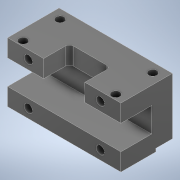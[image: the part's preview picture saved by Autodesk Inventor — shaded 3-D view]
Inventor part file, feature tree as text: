
AUTODESK INVENTOR PART (.ipt)
format: ipt  version: 2021 (Build 250183000, 183)  size: 206,336 bytes
history: native  units: mm
features: sketch x8, other x6, extrude x5, hole x3, fillet x1
ambient origin geometry x8: Origin, YZ Plane, XZ Plane, XY Plane, X Axis, Y Axis, Z Axis, Center Point
bodies: Body1 (feature_tree)
feature tree (23):
  other  "Sólido1"
  extrude  "Extrusão1"  Depth=25.0mm
  extrude  "Extrusão2"  Depth=8.0mm
  extrude  "Extrusão3"  Depth=15.0mm
  extrude  "Extrusão4"  Depth=8.5mm
  hole  "Furo1"  [1 undecoded]
  extrude  "Extrusão5"  Depth=5.0mm
  fillet  "Arredondamento1"  Radius=27.5mm
  hole  "Furo3"  [1 undecoded]
  other  "Plano de trabalho2"
  hole  "Furo4"  [1 undecoded]
  sketch  "Esboço1"  dims[d0=35.0mm d1=25.0mm]
  sketch  "Esboço2"  dims[d2=55.0mm d3=0.0mm d4=8.0mm]
  sketch  "Esboço3"  dims[d5=1.5mm d6=0.0mm d7=15.0mm]
  sketch  "Esboço4"  dims[d8=12.0mm d9=8.5mm]
  sketch  "Esboço5"  dims[d10=0.0mm d11=0.0mm d12=8.5mm]
  other  "Contorno projetado1"
  sketch  "Esboço6"  dims[d13=0.0mm d14=0.0mm d15=5.0mm d16=27.5mm]
  sketch  "Esboço8"  dims[d17=10.0mm d18=10.0mm]
  other  "Contorno projetado4"
  sketch  "Esboço9"  dims[d19=4.0mm d20=6.0mm d21=4.0mm d22=2.0mm d23=90.0deg d24=5.0mm d25=0.0mm d26=20.0mm d27=12.5mm d28=27.5mm d30=2.0mm d31=0.0mm d32=2.0mm d45=2.5mm d46=4.5mm d47=5.0mm d48=5.0mm d49=4.0mm d50=6.0mm d51=4.0mm d52=2.0mm d53=90.0deg d54=5.0mm d55=0.0mm d56=4.25mm d57=10.0mm d58=4.25mm d59=10.0mm d60=4.0mm d61=6.0mm d62=6.0mm d63=2.0mm d64=90.0deg d65=5.0mm d66=0.0mm]
  other  "Contorno projetado5"
  other  "Contorno projetado6"
note: 3 required parameter values undecoded (feature->parameter linkage not recoverable at this tier; creation-order binding heuristic only, values carry confidence <= 0.55)
